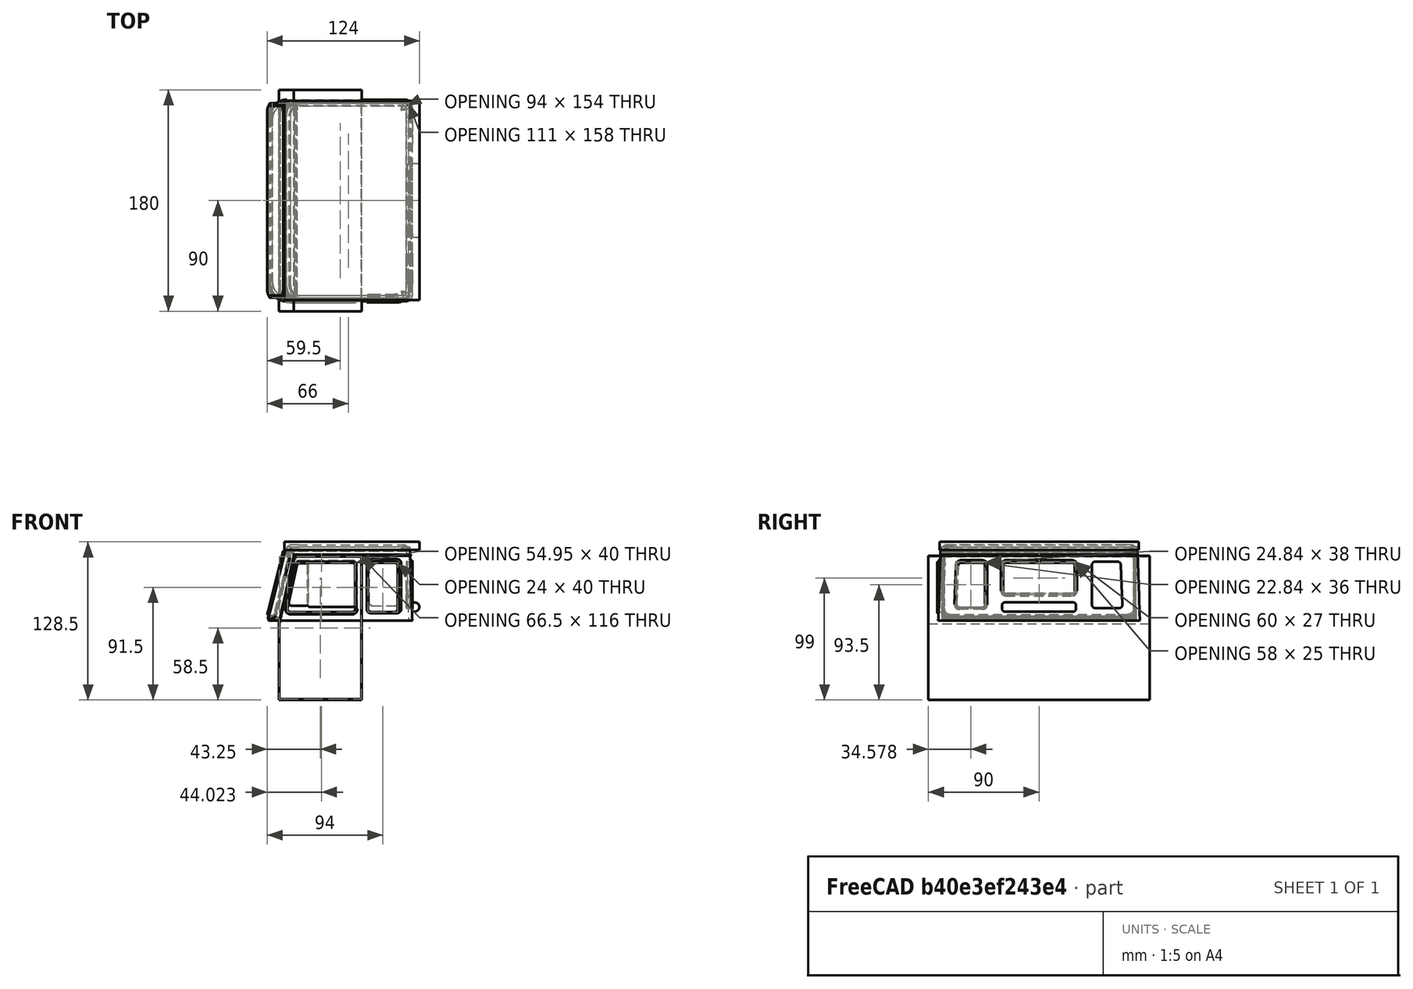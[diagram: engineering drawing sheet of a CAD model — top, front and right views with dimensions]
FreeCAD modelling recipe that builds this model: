
FCSTD DOCUMENT  (FreeCAD 0.15R4640 (Git))
Label: windows
License: All rights reserved
LicenseURL: http://en.wikipedia.org/wiki/All_rights_reserved
objects: Part::Box×58, Part::Fillet×58, Part::Cut×39, Part::Feature×20, Part::Loft×10, Part::MultiFuse×6, Part::Mirroring×1, Part::Cylinder×1
note: 193 computed .brp shape members not serialized (recipe doc carries the construction recipe); baked Part::Feature solids carry a one-line shape summary decoded from their .brp

FEATURE [Part::Feature] Face
  Placement = pos=(0,0,-10) rot=(0,0,1;0rad)
  shape: bbox 128.7 x 180.4 x 2e-07 mm, 1 faces, 0 solids (baked)
FEATURE [Part::Feature] Face001
  Placement = pos=(0,0,50) rot=(0,0,1;0rad)
  shape: bbox 110 x 176 x 2e-07 mm, 1 faces, 0 solids (baked)
FEATURE [Part::Loft] Loft
  Closed = false
  Ruled = false
  Sections = -> [Face001,Face]
  Solid = true
FEATURE [Part::Feature] Face002
  Placement = pos=(0,0,50) rot=(0,0,1;0rad)
  shape: bbox 103.4 x 169.4 x 2e-07 mm, 1 faces, 0 solids (baked)
FEATURE [Part::Feature] Face003
  Placement = pos=(0,0,-10) rot=(0,0,1;0rad)
  shape: bbox 122.1 x 173.8 x 2e-07 mm, 1 faces, 0 solids (baked)
FEATURE [Part::Loft] Loft001
  Closed = false
  Ruled = false
  Sections = -> [Face002,Face003]
  Solid = true
FEATURE [Part::Cut] Cut
  Base = -> Loft
  Tool = -> Loft001
FEATURE [Part::Box] Box  label="Cube340"
  Height = 55
  Length = 10
  Placement = pos=(0,7,69) rot=(0,1,0;0.246091rad)
  Width = 156
FEATURE [Part::Fillet] Fillet
  Base = -> Box
  Edges = 4 edges r=5: [Edge9,Edge10,Edge11,Edge12]
  Placement = pos=(6,0,-1) rot=(0,0,1;0rad)
FEATURE [Part::Box] Box001  label="Cube024"
  Height = 40
  Length = 24
  Placement = pos=(90,4.3,71) rot=(-1,0,0;0.038397rad)
  Width = 5
FEATURE [Part::Fillet] Fillet001
  Base = -> Box001
  Edges = 4 edges r=2.5: [Edge2,Edge4,Edge6,Edge8]
  Placement = pos=(-3,-2,0) rot=(0,0,1;0rad)
FEATURE [Part::Box] Box002  label="Cube048"
  Height = 42
  Length = 58
  Placement = pos=(19.5,3,70) rot=(-1,0,0;0.038397rad)
  Width = 1
FEATURE [Part::Box] Box003  label="Cube049"
  Height = 48
  Length = 11
  Placement = pos=(8.5,1,70) rot=(-0.179679,0.983544,0.018885;0.212918rad)
  Width = 7
FEATURE [Part::Cut] Cut001
  Base = -> Box002
  Tool = -> Box003
FEATURE [Part::Box] Box004  label="Cube362"
  Height = 42
  Length = 26
  Placement = pos=(89,4.3,70) rot=(0,0,1;0rad)
  Width = 1
FEATURE [Part::Fillet] Fillet003
  Base = -> Box004
  Edges = 4 edges r=3: [Edge2,Edge4,Edge6,Edge8]
  Placement = pos=(-3,-2,0) rot=(0,0,1;0rad)
FEATURE [Part::Box] Box005  label="Cube363"
  Height = 42
  Length = 58
  Placement = pos=(19.5,2,70) rot=(0,0,1;0rad)
  Width = 1
FEATURE [Part::Box] Box006  label="Cube364"
  Height = 48
  Length = 11
  Placement = pos=(8.5,-2,70) rot=(-0.179679,0.983544,0.018885;0.212918rad)
  Width = 11
FEATURE [Part::Cut] Cut002
  Base = -> Box005
  Tool = -> Box006
FEATURE [Part::Box] Box007  label="Cube074"
  Height = 27
  Length = 1
  Placement = pos=(118,55,85) rot=(0,0,1;0rad)
  Width = 60
FEATURE [Part::Box] Box008  label="Cube079"
  Height = 38
  Length = 5
  Placement = pos=(175,0,0) rot=(0,0,1;0rad)
  Width = 25
FEATURE [Part::Box] Box009  label="Cube080"
  Height = 40
  Length = 5
  Placement = pos=(175,-24,-1) rot=(-1,0,0;0.038397rad)
  Width = 24
FEATURE [Part::Cut] Cut003
  Base = -> Box008
  Placement = pos=(0,1,1) rot=(0,0,1;0rad)
  Tool = -> Box009
FEATURE [Part::Box] Box010  label="Cube378"
  Height = 38
  Length = 1
  Placement = pos=(175,0,0) rot=(0,0,1;0rad)
  Width = 25
FEATURE [Part::Box] Box011  label="Cube379"
  Height = 40
  Length = 5
  Placement = pos=(175,-24,-1) rot=(-1,0,0;0.038397rad)
  Width = 24
FEATURE [Part::Cut] Cut004
  Base = -> Box010
  Placement = pos=(-57,17,74) rot=(0,0,1;0rad)
  Tool = -> Box011
FEATURE [Part::Mirroring] Part__Mirroring001  label="Cut212"
  Base = (0,0,0)
  Normal = (0,1,0)
  Placement = pos=(-57,154,73) rot=(0,0,1;0rad)
  Source = -> Cut003
FEATURE [Part::Cylinder] Cylinder
  Angle = 360
  Height = 60
  Radius = 3.7
FEATURE [Part::Fillet] Fillet007
  Base = -> Cylinder
  Edges = 2 edges r=2: [Edge1,Edge3]
  Placement = pos=(125,115,75) rot=(1,0,0;1.5708rad)
FEATURE [Part::Box] Box012  label="Cube414"
  Height = 116
  Length = 66.5
  Placement = pos=(14.5,0,-0.5) rot=(0,0,1;0rad)
  Width = 180
FEATURE [Part::Box] Box013  label="Cube416"
  Height = 117
  Length = 67.5
  Placement = pos=(14,0,-1) rot=(0,0,1;0rad)
  Width = 180
FEATURE [Part::Box] Box014  label="Cube415"
  Height = 116
  Length = 67
  Placement = pos=(-53.2,0,65) rot=(0,1,0;0.218166rad)
  Width = 180
FEATURE [Part::Cut] Cut006  label="Cut333"
  Base = -> Box012
  Placement = pos=(0,-2,0) rot=(0,0,1;0rad)
  Tool = -> Box014
FEATURE [Part::Box] Box015  label="Cube417"
  Height = 116
  Length = 67
  Placement = pos=(-53.7,0,65) rot=(0,1,0;0.218166rad)
  Width = 180
FEATURE [Part::Cut] Cut005  label="Cut332"
  Base = -> Box013
  Placement = pos=(0,-2,0) rot=(0,0,1;0rad)
  Tool = -> Box015
FEATURE [Part::Cut] Cut008  label="doors-cut-01"
  Base = -> Cut005
  Placement = pos=(0.5,-3,0.5) rot=(0,0,1;0rad)
  Tool = -> Cut006
FEATURE [Part::Box] Box016  label="Cube437"
  Height = 1
  Length = 96
  Placement = pos=(26,4,116.5) rot=(0,0,1;0rad)
  Width = 162
FEATURE [Part::Box] Box017  label="Cube438"
  Height = 1
  Length = 94
  Placement = pos=(26,6,116.5) rot=(0,0,1;0rad)
  Width = 158
FEATURE [Part::Fillet] Fillet009
  Base = -> Box017
  Edges = 2 edges r=4: [Edge5,Edge7]
FEATURE [Part::Fillet] Fillet010
  Base = -> Box016
  Edges = 2 edges r=6: [Edge5,Edge7]
FEATURE [Part::Fillet] Fillet011
  Base = -> Fillet010
  Edges = 2 edges r=2: [Edge17,Edge18]
FEATURE [Part::Cut] Cut012  label="Cut352"
  Base = -> Fillet011
  Tool = -> Fillet009
FEATURE [Part::Box] Box018  label="Cube439"
  Height = 6.5
  Length = 110
  Placement = pos=(19,4,121.5) rot=(0,0,1;0rad)
  Width = 162
FEATURE [Part::Box] Box019  label="Cube441"
  Height = 5.1
  Length = 100
  Placement = pos=(19.5,5.5,122.5) rot=(0,0,1;0rad)
  Width = 159
FEATURE [Part::Fillet] Fillet012
  Base = -> Box019
  Edges = 2 edges r=10: [Edge1,Edge3]
FEATURE [Part::Fillet] Fillet013
  Base = -> Fillet012
  Edges = 2 edges r=4.5: [Edge17,Edge18]
FEATURE [Part::Fillet] Fillet014
  Base = -> Fillet013
  Edges = 4 edges r=5: [Edge1,Edge4,Edge5,Edge8]
  Placement = pos=(0.7,0,-2) rot=(0,0,1;0rad)
FEATURE [Part::Box] Box020  label="Cube446"
  Height = 5.1
  Length = 95
  Placement = pos=(23,7.5,122.5) rot=(0,0,1;0rad)
  Width = 155
FEATURE [Part::Fillet] Fillet016
  Base = -> Box020
  Edges = 2 edges r=3: [Edge5,Edge7]
FEATURE [Part::Fillet] Fillet017
  Base = -> Fillet016
  Edges = 2 edges r=8: [Edge17,Edge18]
FEATURE [Part::Fillet] Fillet018
  Base = -> Fillet017
  Edges = 1 edges r=4: [Edge4]
  Placement = pos=(0,0,-4) rot=(0,0,1;0rad)
FEATURE [Part::Cut] Cut014  label="Cut354"
  Base = -> Fillet014
  Tool = -> Fillet018
FEATURE [Part::Box] Box021  label="Cube447"
  Height = 44
  Length = 60
  Placement = pos=(18.5,2.6,69) rot=(-1,0,0;0.038397rad)
  Width = 0.5
FEATURE [Part::Box] Box022  label="Cube448"
  Height = 48
  Length = 11
  Placement = pos=(7.5,1,70) rot=(-0.179679,0.983544,0.018885;0.212918rad)
  Width = 7
FEATURE [Part::Cut] Cut015
  Base = -> Box021
  Tool = -> Box022
FEATURE [Part::Box] Box023  label="Cube449"
  Height = 34
  Length = 17
  Placement = pos=(20.5,2,76) rot=(-1,0,0;0.038397rad)
  Width = 5
FEATURE [Part::Box] Box024  label="Cube450"
  Height = 48
  Length = 11
  Placement = pos=(9.5,1,70) rot=(-0.179679,0.983544,0.018885;0.212918rad)
  Width = 7
FEATURE [Part::Cut] Cut016
  Base = -> Box023
  Tool = -> Box024
FEATURE [Part::Fillet] Fillet020
  Base = -> Cut015
  Edges = 4 edges r=4.5: [Edge6,Edge7,Edge8,Edge11]
FEATURE [Part::Fillet] Fillet021
  Base = -> Cut001
  Edges = 4 edges r=3.5: [Edge6,Edge7,Edge8,Edge11]
FEATURE [Part::Box] Box025  label="Cube451"
  Height = 36
  Length = 38
  Placement = pos=(38.5,2,75) rot=(-1,0,0;0.038397rad)
  Width = 5
FEATURE [Part::Fillet] Fillet022
  Base = -> Box025
  Edges = 2 edges r=2.5: [Edge6,Edge8]
FEATURE [Part::Fillet] Fillet023
  Base = -> Fillet022
  Edges = 2 edges r=1: [Edge17,Edge18]
FEATURE [Part::Fillet] Fillet024
  Base = -> Cut016
  Edges = 2 edges r=2.5: [Edge7,Edge11]
FEATURE [Part::Fillet] Fillet025
  Base = -> Fillet024
  Edges = 2 edges r=1: [Edge9,Edge12]
FEATURE [Part::MultiFuse] Fusion002
  Shapes = -> [Fillet023,Fillet025]
FEATURE [Part::MultiFuse] Fusion
  Shapes = -> [Fillet020,Fillet021]
FEATURE [Part::Cut] Cut017
  Base = -> Fusion
  Tool = -> Fusion002
FEATURE [Part::Fillet] Fillet026
  Base = -> Cut017
  Edges = 2 edges r=0.49: [Edge16,Edge24]
FEATURE [Part::Fillet] Fillet027  label="left-front-window-border"
  Base = -> Fillet026
  Edges = 1 edges r=0.49: [Edge9]
FEATURE [Part::Box] Box026  label="Cube452"
  Height = 44
  Length = 28
  Placement = pos=(89,4.3,70) rot=(-1,0,0;0.038397rad)
  Width = 0.5
FEATURE [Part::Fillet] Fillet028
  Base = -> Box026
  Edges = 4 edges r=3.5: [Edge2,Edge4,Edge6,Edge8]
  Placement = pos=(-3,-2,0) rot=(0,0,1;0rad)
FEATURE [Part::Box] Box027  label="Cube453"
  Height = 36
  Length = 24
  Placement = pos=(89,4.3,74) rot=(-1,0,0;0.038397rad)
  Width = 6
FEATURE [Part::Fillet] Fillet029
  Base = -> Box027
  Edges = 4 edges r=2.5: [Edge2,Edge4,Edge6,Edge8]
  Placement = pos=(-1,-2,2) rot=(0,0,1;0rad)
FEATURE [Part::Box] Box028  label="Cube454"
  Height = 42
  Length = 26
  Placement = pos=(90,4.3,71) rot=(-1,0,0;0.038397rad)
  Width = 1
FEATURE [Part::Fillet] Fillet030
  Base = -> Box028
  Edges = 4 edges r=3: [Edge2,Edge4,Edge6,Edge8]
  Placement = pos=(-3,-1.5,0) rot=(0,0,1;0rad)
FEATURE [Part::MultiFuse] Fusion003
  Shapes = -> [Fillet028,Fillet030]
FEATURE [Part::Cut] Cut018
  Base = -> Fusion003
  Tool = -> Fillet029
FEATURE [Part::Fillet] Fillet031
  Base = -> Cut018
  Edges = 2 edges r=0.49: [Edge1,Edge17]
FEATURE [Part::Box] Box032  label="Cube458"
  Height = 53
  Length = 10
  Placement = pos=(0,8,70) rot=(0,1,0;0.246091rad)
  Width = 154
FEATURE [Part::Fillet] Fillet034
  Base = -> Box032
  Edges = 4 edges r=5: [Edge9,Edge10,Edge11,Edge12]
  Placement = pos=(5,0,-1) rot=(0,0,1;0rad)
FEATURE [Part::Box] Box033  label="Cube459"
  Height = 53
  Length = 10
  Placement = pos=(0,8,70) rot=(0,1,0;0.246091rad)
  Width = 154
FEATURE [Part::Fillet] Fillet035
  Base = -> Box033
  Edges = 4 edges r=5: [Edge9,Edge10,Edge11,Edge12]
  Placement = pos=(6,0,-1) rot=(0,0,1;0rad)
FEATURE [Part::Box] Box034  label="Cube460"
  Height = 55
  Length = 10
  Placement = pos=(0,7,68) rot=(0,1,0;0.226893rad)
  Width = 156
FEATURE [Part::Fillet] Fillet036
  Base = -> Box034
  Edges = 4 edges r=5: [Edge9,Edge10,Edge11,Edge12]
  Placement = pos=(6,0,-1) rot=(0,0,1;0rad)
FEATURE [Part::Cut] Cut023
  Base = -> Cut
  Tool = -> Fillet036
FEATURE [Part::Box] Box035  label="Cube461"
  Height = 57
  Length = 8
  Placement = pos=(-0.5,6,67) rot=(0,1,0;0.244346rad)
  Width = 158
FEATURE [Part::Fillet] Fillet037
  Base = -> Box035
  Edges = 4 edges r=5: [Edge9,Edge10,Edge11,Edge12]
  Placement = pos=(6,0,-1) rot=(0,0,1;0rad)
FEATURE [Part::Box] Box036  label="Cube462"
  Height = 57
  Length = 10
  Placement = pos=(0,6,67) rot=(0,1,0;0.244346rad)
  Width = 158
FEATURE [Part::Fillet] Fillet038
  Base = -> Box036
  Edges = 4 edges r=5: [Edge9,Edge10,Edge11,Edge12]
  Placement = pos=(6,0,-1) rot=(0,0,1;0rad)
FEATURE [Part::Feature] Face004
  Placement = pos=(0,0,-10) rot=(0,0,1;0rad)
  shape: bbox 128.7 x 180.4 x 2e-07 mm, 1 faces, 0 solids (baked)
FEATURE [Part::Feature] Face005
  Placement = pos=(0,0,50) rot=(0,0,1;0rad)
  shape: bbox 110 x 176 x 2e-07 mm, 1 faces, 0 solids (baked)
FEATURE [Part::Loft] Loft002
  Closed = false
  Ruled = false
  Sections = -> [Face005,Face004]
  Solid = true
FEATURE [Part::Cut] Cut024
  Base = -> Fillet037
  Tool = -> Loft002
FEATURE [Part::Box] Box037  label="Cube463"
  Height = 57
  Length = 6.5
  Placement = pos=(-0.5,6,67) rot=(0,1,0;0.244346rad)
  Width = 158
FEATURE [Part::Fillet] Fillet039
  Base = -> Box037
  Edges = 4 edges r=5: [Edge9,Edge10,Edge11,Edge12]
  Placement = pos=(6,0,-1) rot=(0,0,1;0rad)
FEATURE [Part::Cut] Cut025
  Base = -> Fillet039
  Placement = pos=(-1,0,0) rot=(0,0,1;0rad)
  Tool = -> Cut024
FEATURE [Part::Feature] Face006
  Placement = pos=(0,0,-10) rot=(0,0,1;0rad)
  shape: bbox 128.7 x 180.4 x 2e-07 mm, 1 faces, 0 solids (baked)
FEATURE [Part::Feature] Face007
  Placement = pos=(0,0,50) rot=(0,0,1;0rad)
  shape: bbox 110 x 176 x 2e-07 mm, 1 faces, 0 solids (baked)
FEATURE [Part::Loft] Loft003
  Closed = false
  Ruled = false
  Sections = -> [Face007,Face006]
  Solid = true
FEATURE [Part::Cut] Cut026
  Base = -> Cut025
  Tool = -> Loft003
FEATURE [Part::Box] Box038  label="Cube464"
  Height = 55
  Length = 10
  Placement = pos=(0,7,68) rot=(0,1,0;0.244346rad)
  Width = 156
FEATURE [Part::Fillet] Fillet040
  Base = -> Box038
  Edges = 4 edges r=5: [Edge9,Edge10,Edge11,Edge12]
  Placement = pos=(5,0,-1) rot=(0,0,1;0rad)
FEATURE [Part::Cut] Cut027
  Base = -> Cut026
  Tool = -> Fillet040
FEATURE [Part::Box] Box039  label="Cube465"
  Height = 55
  Length = 6
  Placement = pos=(0,7,68) rot=(0,1,0;0.244346rad)
  Width = 156
FEATURE [Part::Fillet] Fillet041
  Base = -> Box039
  Edges = 4 edges r=5: [Edge9,Edge10,Edge11,Edge12]
  Placement = pos=(6,0,-1) rot=(0,0,1;0rad)
FEATURE [Part::Box] Box040  label="Cube466"
  Height = 57
  Length = 8
  Placement = pos=(-0.5,6,67) rot=(0,1,0;0.244346rad)
  Width = 158
FEATURE [Part::Fillet] Fillet042
  Base = -> Box040
  Edges = 4 edges r=5: [Edge9,Edge10,Edge11,Edge12]
  Placement = pos=(6,0,-1) rot=(0,0,1;0rad)
FEATURE [Part::Feature] Face008
  Placement = pos=(0,0,50) rot=(0,0,1;0rad)
  shape: bbox 110 x 176 x 2e-07 mm, 1 faces, 0 solids (baked)
FEATURE [Part::Feature] Face009
  Placement = pos=(0,0,-10) rot=(0,0,1;0rad)
  shape: bbox 128.7 x 180.4 x 2e-07 mm, 1 faces, 0 solids (baked)
FEATURE [Part::Loft] Loft004
  Closed = false
  Ruled = false
  Sections = -> [Face008,Face009]
  Solid = true
FEATURE [Part::Cut] Cut029
  Base = -> Fillet042
  Tool = -> Loft004
FEATURE [Part::Cut] Cut028
  Base = -> Fillet041
  Placement = pos=(-1,0,0) rot=(0,0,1;0rad)
  Tool = -> Cut029
FEATURE [Part::Feature] Face010
  Placement = pos=(0,0,50) rot=(0,0,1;0rad)
  shape: bbox 110 x 176 x 2e-07 mm, 1 faces, 0 solids (baked)
FEATURE [Part::Feature] Face011
  Placement = pos=(0,0,-10) rot=(0,0,1;0rad)
  shape: bbox 128.7 x 180.4 x 2e-07 mm, 1 faces, 0 solids (baked)
FEATURE [Part::Loft] Loft005
  Closed = false
  Placement = pos=(1,0,0) rot=(0,0,1;0rad)
  Ruled = false
  Sections = -> [Face010,Face011]
  Solid = true
FEATURE [Part::Cut] Cut030
  Base = -> Cut028
  Tool = -> Loft005
FEATURE [Part::MultiFuse] Fusion004
  Shapes = -> [Cut027,Cut030]
FEATURE [Part::Box] Box041  label="Cube467"
  Height = 53
  Length = 10
  Placement = pos=(-1,8,69) rot=(0,1,0;0.244346rad)
  Width = 154
FEATURE [Part::Fillet] Fillet043
  Base = -> Box041
  Edges = 4 edges r=5: [Edge9,Edge10,Edge11,Edge12]
  Placement = pos=(6,0,-1) rot=(0,0,1;0rad)
FEATURE [Part::Cut] Cut031
  Base = -> Fusion004
  Tool = -> Fillet043
FEATURE [Part::Fillet] Fillet044
  Base = -> Cut031
  Edges = 1 edges r=1: [Edge49]
FEATURE [Part::Fillet] Fillet045
  Base = -> Box007
  Edges = 4 edges r=3: [Edge9,Edge10,Edge11,Edge12]
FEATURE [Part::Fillet] Fillet046
  Base = -> Part__Mirroring001
  Edges = 4 edges r=3: [Edge1,Edge3,Edge5,Edge10]
FEATURE [Part::Fillet] Fillet047
  Base = -> Cut004
  Edges = 4 edges r=3: [Edge5,Edge7,Edge8,Edge11]
FEATURE [Part::Box] Box042  label="Cube468"
  Height = 40
  Length = 1
  Placement = pos=(175,0,0) rot=(0,0,1;0rad)
  Width = 27
FEATURE [Part::Box] Box043  label="Cube469"
  Height = 42
  Length = 5
  Placement = pos=(175,-24,-1) rot=(-1,0,0;0.038397rad)
  Width = 24
FEATURE [Part::Cut] Cut032
  Base = -> Box042
  Placement = pos=(-57,16,73) rot=(0,0,1;0rad)
  Tool = -> Box043
FEATURE [Part::Fillet] Fillet048
  Base = -> Cut032
  Edges = 4 edges r=4: [Edge5,Edge7,Edge8,Edge11]
  Placement = pos=(4,0,0) rot=(0,0,1;0rad)
FEATURE [Part::Box] Box044  label="Cube470"
  Height = 38
  Length = 2
  Placement = pos=(175,0,0) rot=(0,0,1;0rad)
  Width = 25
FEATURE [Part::Box] Box045  label="Cube471"
  Height = 40
  Length = 5
  Placement = pos=(175,-24,-1) rot=(-1,0,0;0.038397rad)
  Width = 24
FEATURE [Part::Cut] Cut033
  Base = -> Box044
  Placement = pos=(-57,17,74) rot=(0,0,1;0rad)
  Tool = -> Box045
FEATURE [Part::Fillet] Fillet049
  Base = -> Cut033
  Edges = 4 edges r=3: [Edge5,Edge7,Edge8,Edge11]
  Placement = pos=(3,0,0) rot=(0,0,1;0rad)
FEATURE [Part::Box] Box046  label="Cube472"
  Height = 36
  Length = 5
  Placement = pos=(175,0,0) rot=(0,0,1;0rad)
  Width = 23
FEATURE [Part::Box] Box047  label="Cube473"
  Height = 40
  Length = 5
  Placement = pos=(175,-24,-1) rot=(-1,0,0;0.038397rad)
  Width = 24
FEATURE [Part::Cut] Cut034
  Base = -> Box046
  Placement = pos=(-57,17,74) rot=(0,0,1;0rad)
  Tool = -> Box047
FEATURE [Part::Fillet] Fillet050
  Base = -> Cut034
  Edges = 4 edges r=2.5: [Edge5,Edge7,Edge8,Edge11]
  Placement = pos=(0,1,1) rot=(0,0,1;0rad)
FEATURE [Part::MultiFuse] Fusion005
  Shapes = -> [Fillet048,Fillet049]
FEATURE [Part::Cut] Cut035
  Base = -> Fusion005
  Tool = -> Fillet050
FEATURE [Part::Fillet] Fillet051
  Base = -> Cut035
  Edges = 2 edges r=1: [Edge29,Edge33]
FEATURE [Part::Fillet] Fillet052
  Base = -> Fillet051
  Edges = 2 edges r=0.8: [Edge12,Edge13]
FEATURE [Part::Box] Box048  label="Cube474"
  Height = 25
  Length = 5
  Placement = pos=(118,56,86) rot=(0,0,1;0rad)
  Width = 58
FEATURE [Part::Fillet] Fillet053
  Base = -> Box048
  Edges = 4 edges r=2: [Edge9,Edge10,Edge11,Edge12]
FEATURE [Part::Box] Box049  label="Cube475"
  Height = 27
  Length = 2
  Placement = pos=(118,55,85) rot=(0,0,1;0rad)
  Width = 60
FEATURE [Part::Fillet] Fillet054
  Base = -> Box049
  Edges = 4 edges r=3: [Edge9,Edge10,Edge11,Edge12]
  Placement = pos=(3,0,0) rot=(0,0,1;0rad)
FEATURE [Part::Box] Box050  label="Cube476"
  Height = 29
  Length = 1
  Placement = pos=(118,54,84) rot=(0,0,1;0rad)
  Width = 62
FEATURE [Part::Fillet] Fillet055
  Base = -> Box050
  Edges = 4 edges r=4: [Edge9,Edge10,Edge11,Edge12]
  Placement = pos=(4,0,0) rot=(0,0,1;0rad)
FEATURE [Part::MultiFuse] Fusion006
  Shapes = -> [Fillet054,Fillet055]
FEATURE [Part::Cut] Cut036
  Base = -> Fusion006
  Tool = -> Fillet053
FEATURE [Part::Fillet] Fillet056
  Base = -> Cut036
  Edges = 2 edges r=1: [Edge40,Edge48]
FEATURE [Part::Fillet] Fillet057
  Base = -> Fillet056
  Edges = 2 edges r=0.99: [Edge40,Edge41]
FEATURE [Part::Fillet] Fillet058
  Base = -> Cut002
  Edges = 4 edges r=3: [Edge6,Edge7,Edge8,Edge11]
FEATURE [Part::Box] Box051  label="Cube477"
  Height = 40
  Length = 24
  Placement = pos=(90,4.3,71) rot=(0,0,1;0rad)
  Width = 5
FEATURE [Part::Fillet] Fillet059
  Base = -> Box051
  Edges = 4 edges r=2: [Edge2,Edge4,Edge6,Edge8]
  Placement = pos=(-3,-2,0) rot=(0,0,1;0rad)
FEATURE [Part::Cut] Cut037
  Base = -> Fillet003
  Tool = -> Fillet059
FEATURE [Part::Box] Box052  label="Cube478"
  Height = 48
  Length = 11
  Placement = pos=(9.5,-2,70) rot=(-0.179679,0.983544,0.018885;0.212918rad)
  Width = 11
FEATURE [Part::Box] Box053  label="Cube479"
  Height = 40
  Length = 57
  Placement = pos=(19.5,2,71) rot=(0,0,1;0rad)
  Width = 5
FEATURE [Part::Cut] Cut038
  Base = -> Box053
  Tool = -> Box052
FEATURE [Part::Fillet] Fillet060
  Base = -> Cut038
  Edges = 4 edges r=2.5: [Edge6,Edge7,Edge8,Edge11]
FEATURE [Part::Cut] Cut039
  Base = -> Fillet058
  Tool = -> Fillet060
FEATURE [Part::Box] Box054  label="Cube480"
  Height = 36
  Length = 1
  Placement = pos=(175,1,1) rot=(0,0,1;0rad)
  Width = 23
FEATURE [Part::Box] Box055  label="Cube481"
  Height = 40
  Length = 5
  Placement = pos=(175,-23,-1) rot=(-1,0,0;0.038397rad)
  Width = 24
FEATURE [Part::Cut] Cut040
  Base = -> Box054
  Placement = pos=(-57,17,74) rot=(0,0,1;0rad)
  Tool = -> Box055
FEATURE [Part::Fillet] Fillet061
  Base = -> Cut040
  Edges = 4 edges r=2.5: [Edge5,Edge7,Edge8,Edge11]
FEATURE [Part::Cut] Cut041
  Base = -> Fillet047
  Tool = -> Fillet061
FEATURE [Part::Box] Box056  label="Cube482"
  Height = 25
  Length = 5
  Placement = pos=(118,56,86) rot=(0,0,1;0rad)
  Width = 58
FEATURE [Part::Fillet] Fillet062
  Base = -> Box056
  Edges = 4 edges r=2.5: [Edge9,Edge10,Edge11,Edge12]
FEATURE [Part::Cut] Cut042
  Base = -> Fillet045
  Tool = -> Fillet062
FEATURE [Part::Box] Box057  label="Cube483"
  Height = 55
  Length = 10
  Placement = pos=(0,7,68) rot=(0,1,0;0.226893rad)
  Width = 156
FEATURE [Part::Fillet] Fillet063
  Base = -> Box057
  Edges = 4 edges r=5: [Edge9,Edge10,Edge11,Edge12]
  Placement = pos=(6,0,-1) rot=(0,0,1;0rad)
FEATURE [Part::Feature] Face012
  Placement = pos=(0,0,-10) rot=(0,0,1;0rad)
  shape: bbox 128.7 x 180.4 x 2e-07 mm, 1 faces, 0 solids (baked)
FEATURE [Part::Feature] Face013
  Placement = pos=(0,0,50) rot=(0,0,1;0rad)
  shape: bbox 110 x 176 x 2e-07 mm, 1 faces, 0 solids (baked)
FEATURE [Part::Loft] Loft006
  Closed = false
  Ruled = false
  Sections = -> [Face013,Face012]
  Solid = true
FEATURE [Part::Feature] Face014
  Placement = pos=(0,0,50) rot=(0,0,1;0rad)
  shape: bbox 103.4 x 169.4 x 2e-07 mm, 1 faces, 0 solids (baked)
FEATURE [Part::Feature] Face015
  Placement = pos=(0,0,-10) rot=(0,0,1;0rad)
  shape: bbox 122.1 x 173.8 x 2e-07 mm, 1 faces, 0 solids (baked)
FEATURE [Part::Loft] Loft007
  Closed = false
  Ruled = false
  Sections = -> [Face014,Face015]
  Solid = true
FEATURE [Part::Cut] Cut043
  Base = -> Loft006
  Tool = -> Loft007
FEATURE [Part::Feature] Face016
  Placement = pos=(0,0,-10) rot=(0,0,1;0rad)
  shape: bbox 128.7 x 180.4 x 2e-07 mm, 1 faces, 0 solids (baked)
FEATURE [Part::Feature] Face017
  Placement = pos=(0,0,50) rot=(0,0,1;0rad)
  shape: bbox 110 x 176 x 2e-07 mm, 1 faces, 0 solids (baked)
FEATURE [Part::Loft] Loft008
  Closed = false
  Ruled = false
  Sections = -> [Face017,Face016]
  Solid = true
FEATURE [Part::Box] Box058  label="Cube484"
  Height = 55
  Length = 10
  Placement = pos=(0,7,68) rot=(0,1,0;0.226893rad)
  Width = 156
FEATURE [Part::Fillet] Fillet064
  Base = -> Box058
  Edges = 4 edges r=5: [Edge9,Edge10,Edge11,Edge12]
  Placement = pos=(6,0,-1) rot=(0,0,1;0rad)
FEATURE [Part::Cut] Cut044
  Base = -> Fillet064
  Tool = -> Loft008
FEATURE [Part::Box] Box059  label="Cube485"
  Height = 55
  Length = 10
  Placement = pos=(0,7,68) rot=(0,1,0;0.226893rad)
  Width = 156
FEATURE [Part::Fillet] Fillet065
  Base = -> Box059
  Edges = 4 edges r=5: [Edge9,Edge10,Edge11,Edge12]
  Placement = pos=(6,0,-1) rot=(0,0,1;0rad)
FEATURE [Part::Cut] Cut045
  Base = -> Fillet065
  Tool = -> Cut044
FEATURE [Part::Feature] Face018
  Placement = pos=(0,0,-10) rot=(0,0,1;0rad)
  shape: bbox 128.7 x 180.4 x 2e-07 mm, 1 faces, 0 solids (baked)
FEATURE [Part::Feature] Face019
  Placement = pos=(0,0,50) rot=(0,0,1;0rad)
  shape: bbox 110 x 176 x 2e-07 mm, 1 faces, 0 solids (baked)
FEATURE [Part::Loft] Loft009
  Closed = false
  Placement = pos=(1,0,0) rot=(0,0,1;0rad)
  Ruled = false
  Sections = -> [Face019,Face018]
  Solid = true
FEATURE [Part::Box] Box060  label="Cube486"
  Height = 53
  Length = 10
  Placement = pos=(0,7.7,69) rot=(0,1,0;0.226893rad)
  Width = 154.6
FEATURE [Part::Fillet] Fillet066
  Base = -> Box060
  Edges = 4 edges r=4.5: [Edge9,Edge10,Edge11,Edge12]
  Placement = pos=(6,0,-1) rot=(0,0,1;0rad)
FEATURE [Part::Cut] Cut046
  Base = -> Cut045
  Tool = -> Loft009
FEATURE [Part::Cut] Cut047
  Base = -> Cut046
  Tool = -> Fillet066
